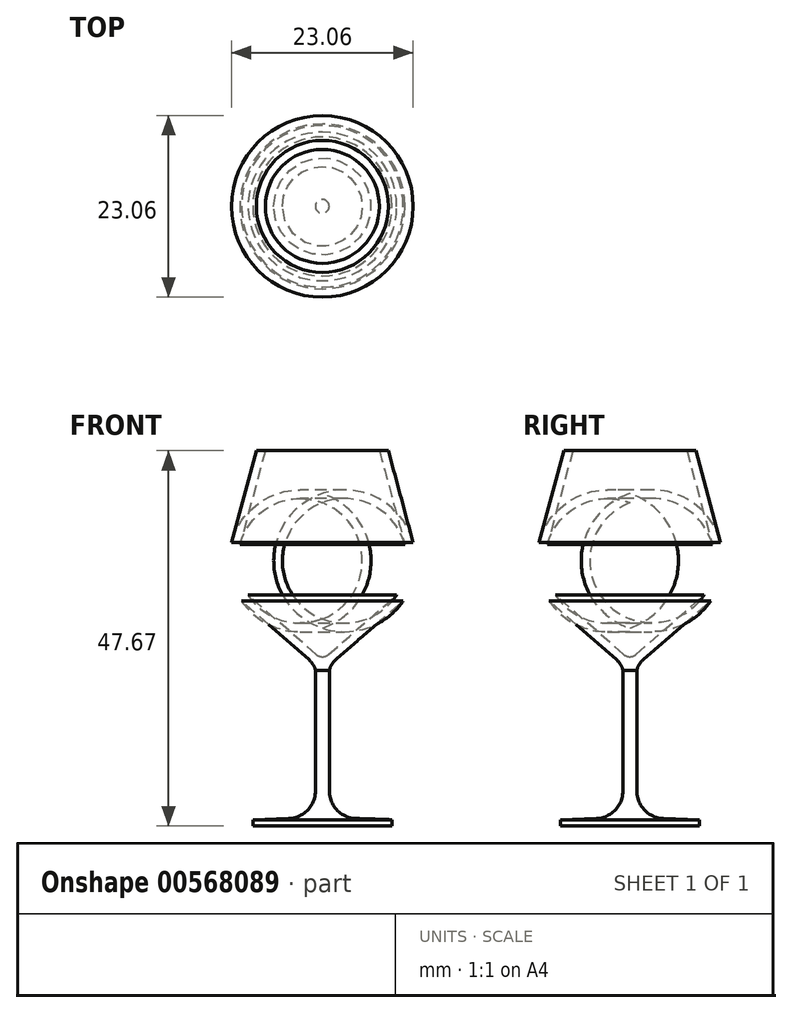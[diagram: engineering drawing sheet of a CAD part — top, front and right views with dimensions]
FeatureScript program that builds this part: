
annotation { "Feature Type Name" : "Feature", "Feature Type Description" : "" }
export const myFeature = defineFeature(function(context is Context, id is Id, definition is map)
    precondition{}
    {
        {
            var Q0;
            Q0=qCreatedBy(makeId("Front.planeOp"),FACE);
            var sketch = newSketch(context, id + "F0", { "sketchPlane" : qUnion([Q0])});
            skLineSegment(sketch, "E0", {"start": v(8.38, 48.55) * mm, "end": v(11.53, 36.9) * mm});
            skArc(sketch, "E1", {"start": v(10.27, 29.47) * mm, "mid": v(11.72, 33.05) * mm, "end": v(11.53, 36.9) * mm});
            skLineSegment(sketch, "E2", {"start": v(10.27, 29.47) * mm, "end": v(1.7, 22) * mm});
            skArc(sketch, "E3", {"start": v(1.7, 22) * mm, "mid": v(1.2, 21.39) * mm, "end": v(0.88, 20.65) * mm});
            skLineSegment(sketch, "E4", {"start": v(0.88, 20.65) * mm, "end": v(0.88, 5.32) * mm});
            skArc(sketch, "E5", {"start": v(0.88, 5.32) * mm, "mid": v(1.87, 2.88) * mm, "end": v(4.27, 1.82) * mm});
            skLineSegment(sketch, "E6", {"start": v(0, 0) * mm, "end": v(0, 49.63) * mm});
            skLineSegment(sketch, "E7", {"start": v(0, 70.13) * mm, "end": v(0, -23.56) * mm, "construction": true});
            skLineSegment(sketch, "E8", {"start": v(4.27, 1.82) * mm, "end": v(8.83, 1.67) * mm});
            skLineSegment(sketch, "E9", {"start": v(8.83, 1.67) * mm, "end": v(8.83, 0.88) * mm});
            skLineSegment(sketch, "E10", {"start": v(8.83, 0.88) * mm, "end": v(0, 0.88) * mm});
            skLineSegment(sketch, "E11.0", {"start": v(9.44, 30.2) * mm, "end": v(0.8, 22.66) * mm});
            skArc(sketch, "E11.1", {"start": v(9.44, 30.2) * mm, "mid": v(10.64, 33.3) * mm, "end": v(10.47, 36.62) * mm});
            skLineSegment(sketch, "E11.2", {"start": v(7.24, 48.55) * mm, "end": v(10.47, 36.62) * mm});
            skArc(sketch, "E12", {"start": v(0, 22.36) * mm, "mid": v(0.42, 22.44) * mm, "end": v(0.8, 22.66) * mm});
            skLineSegment(sketch, "E13", {"start": v(7.24, 48.55) * mm, "end": v(8.38, 48.55) * mm});
            skLineSegment(sketch, "E14", {"start": v(0, 22.36) * mm, "end": v(0, 0.88) * mm});
            skSolve(sketch);
        }
        {
            var Q0;
            Q0 = qSketchRegion(id + "F0", true);
            var Q1;
            Q1=sQuery(id+"F0.wireOp",EDGE,"E7");
            revolve(context, id + "F1", {"entities" : qUnion([Q0]), "axis" : qUnion([Q1]), "revolveType" : RevolveType.FULL});
        }
    });
